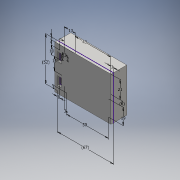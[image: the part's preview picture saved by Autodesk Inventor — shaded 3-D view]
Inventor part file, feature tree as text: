
AUTODESK INVENTOR PART (.ipt)
format: ipt  version: 2016 (Build 200138000, 138)  size: 158,720 bytes
history: native  units: mm
features: extrude x4, sketch x2
ambient origin geometry x8: Origin, YZ Plane, XZ Plane, XY Plane, X Axis, Y Axis, Z Axis, Center Point
bodies: Solid1 (feature_tree)
feature tree (6):
  sketch  "Sketch1"  dims[d3=15.0mm d5=10.0mm]
  extrude  "Extrusion1"  Depth=10.0mm
  sketch  "Sketch2"  dims[d6=5.0mm d11=50.0mm d12=3.0mm d13=43.0mm d14=13.0mm d15=16.0mm d16=0.0mm d22=19.0mm d23=21.0mm d26=3.0mm d27=3.0mm d28=3.0mm d29=3.0mm d30=6.0mm d31=67.0mm d32=52.0mm d33=8.0mm d34=3.0mm d35=2.0mm d38=13.0mm d39=0.0mm d40=10.0mm d41=0.0mm d42=3.0mm d43=0.0mm]
  extrude  "Extrusion4"  Depth=50.0mm
  extrude  "Extrusion5"  Depth=3.0mm
  extrude  "Extrusion6"  Depth=43.0mm
